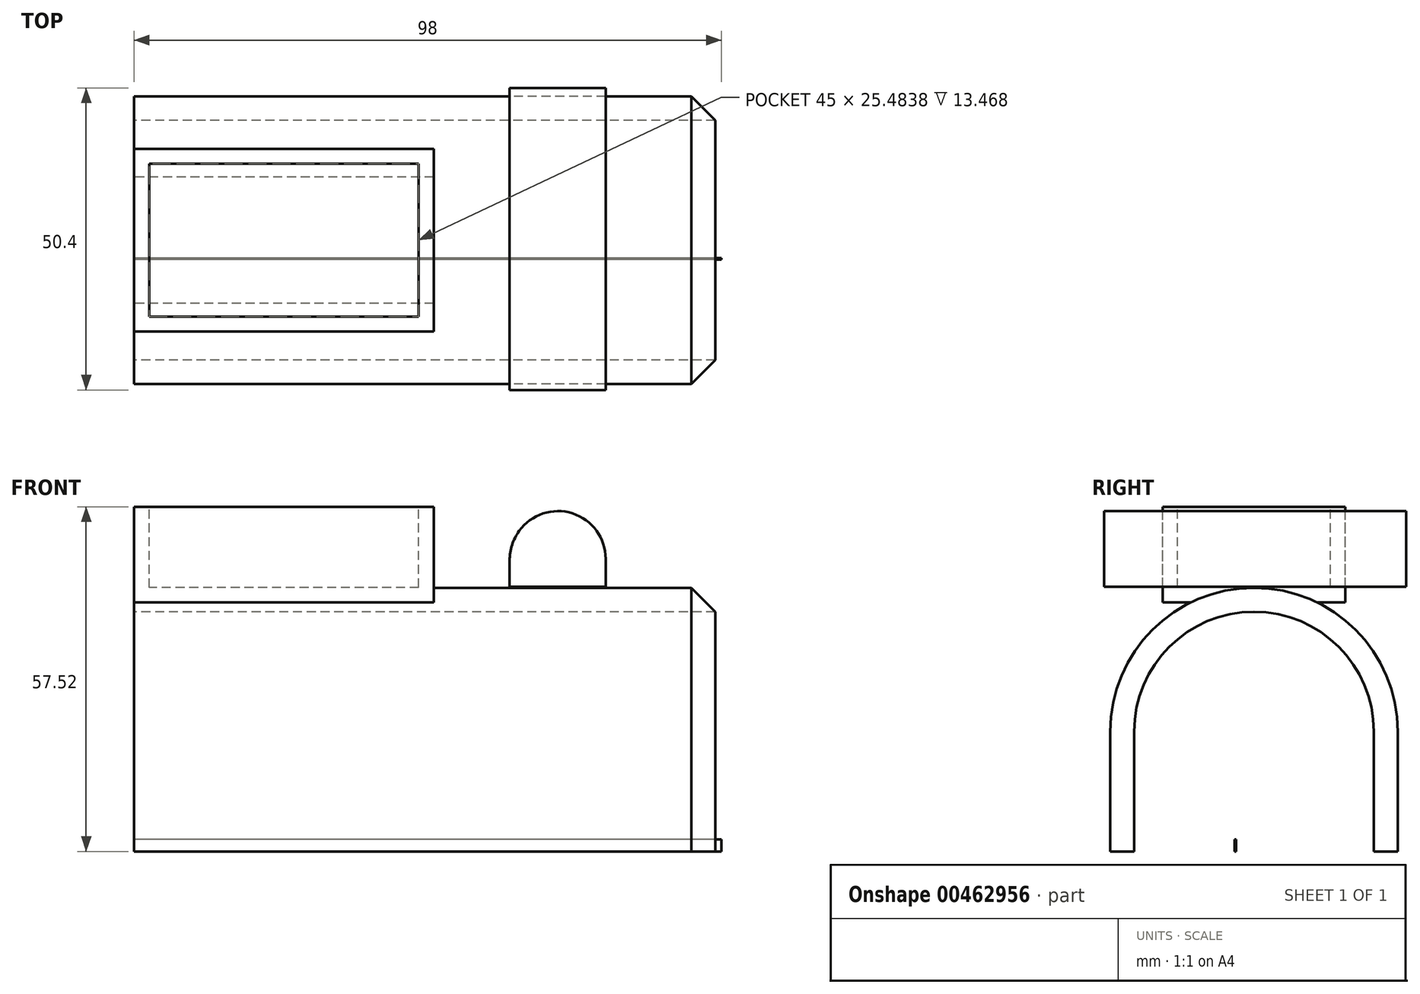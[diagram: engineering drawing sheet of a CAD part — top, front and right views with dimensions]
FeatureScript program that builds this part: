
annotation { "Feature Type Name" : "Feature", "Feature Type Description" : "" }
export const myFeature = defineFeature(function(context is Context, id is Id, definition is map)
    precondition{}
    {
        {
            var Q0;
            Q0=qCreatedBy(makeId("Right.planeOp"),FACE);
            var sketch = newSketch(context, id + "F0", { "sketchPlane" : qUnion([Q0])});
            skLineSegment(sketch, "E0.bottom", {"start": v(-3.25, 0) * mm, "end": v(-3, 0) * mm});
            skLineSegment(sketch, "E0.top", {"start": v(-3.25, 2) * mm, "end": v(-3, 2) * mm});
            skLineSegment(sketch, "E0.left", {"start": v(-3.25, 0) * mm, "end": v(-3.25, 2) * mm});
            skLineSegment(sketch, "E0.right", {"start": v(-3, 0) * mm, "end": v(-3, 2) * mm});
            skSolve(sketch);
        }
        {
            var Q0;
            Q0=qCreatedBy(makeId("Right.planeOp"),FACE);
            var sketch = newSketch(context, id + "F1", { "sketchPlane" : qUnion([Q0])});
            skLineSegment(sketch, "E1.bottom", {"start": v(-20, 0) * mm, "end": v(-24, 0) * mm});
            skLineSegment(sketch, "E1.top", {"start": v(-20, 20) * mm, "end": v(-24, 20) * mm});
            skLineSegment(sketch, "E1.left", {"start": v(-20, 0) * mm, "end": v(-20, 20) * mm});
            skLineSegment(sketch, "E1.right", {"start": v(-24, 0) * mm, "end": v(-24, 20) * mm});
            skLineSegment(sketch, "E2.MirrorCS", {"start": v(20, 0) * mm, "end": v(24, 0) * mm});
            skLineSegment(sketch, "E3.MirrorCS", {"start": v(20, 20) * mm, "end": v(24, 20) * mm});
            skLineSegment(sketch, "E4.MirrorCS", {"start": v(24, 0) * mm, "end": v(24, 20) * mm});
            skLineSegment(sketch, "E5.MirrorCS", {"start": v(20, 0) * mm, "end": v(20, 20) * mm});
            skArc(sketch, "E6", {"start": v(20, 20) * mm, "mid": v(0, 40) * mm, "end": v(-20, 20) * mm});
            skArc(sketch, "E7", {"start": v(24, 20) * mm, "mid": v(0, 44) * mm, "end": v(-24, 20) * mm});
            skSolve(sketch);
        }
        {
            var Q0;
            Q0=makeQuery(id+"F1.imprint","IMPRINT",FACE,{"disambiguationData":[TD([[makeQuery(id+"F1.imprint","IMPRINT",EDGE,{"derivedFrom":sQuery(id+"F1.wireOp",EDGE,"E1.bottom")}),-1.0]])]});
            var Q1;
            Q1=makeQuery(id+"F1.imprint","IMPRINT",FACE,{"disambiguationData":[TD([[makeQuery(id+"F1.imprint","IMPRINT",EDGE,{"derivedFrom":sQuery(id+"F1.wireOp",EDGE,"E2.MirrorCS")}),1.0]])]});
            var Q2;
            Q2=makeQuery(id+"F1.imprint","IMPRINT",FACE,{"disambiguationData":[TD([[makeQuery(id+"F1.imprint","IMPRINT",EDGE,{"derivedFrom":sQuery(id+"F1.wireOp",EDGE,"E1.top")}),-1.0]])]});
            var Q3;
            Q3=makeQuery(id+"F0.imprint","IMPRINT",FACE,{"disambiguationData":[TD([[makeQuery(id+"F0.imprint","IMPRINT",EDGE,{"derivedFrom":sQuery(id+"F0.wireOp",EDGE,"E0.bottom")}),1.0]])]});
            extrude(context, id + "F2", {"entities" : qUnion([Q0, Q1, Q2, Q3]), "depth" : 98 * mm});
        }
        {
            var Q0;
            Q0=qCreatedBy(makeId("Right.planeOp"),FACE);
            var sketch = newSketch(context, id + "F3", { "sketchPlane" : qUnion([Q0])});
            skLineSegment(sketch, "E8.bottom", {"start": v(15.24, 41.55) * mm, "end": v(-15.24, 41.55) * mm});
            skLineSegment(sketch, "E8.top", {"start": v(15.24, 57.52) * mm, "end": v(-15.24, 57.52) * mm});
            skLineSegment(sketch, "E8.left", {"start": v(15.24, 41.55) * mm, "end": v(15.24, 57.52) * mm});
            skLineSegment(sketch, "E8.right", {"start": v(-15.24, 41.55) * mm, "end": v(-15.24, 57.52) * mm});
            skPoint(sketch, "E8.middle", {"position": v(0, 49.54) * mm});
            skSolve(sketch);
        }
        {
            var Q0;
            Q0=makeQuery(id+"F2.opExtrude","CAP_EDGE",EDGE,{"disambiguationData":[OSD([sQuery(id+"F1.wireOp",EDGE,"E7")])],"isStart":false});
            chamfer(context, id + "F4", {"entities" : qUnion([Q0]), "width" : 5 * mm, "tangentPropagation" : true});
        }
        {
            var Q0;
            Q0=makeQuery(id+"F3.imprint","IMPRINT",FACE,{"disambiguationData":[TD([[makeQuery(id+"F3.imprint","IMPRINT",EDGE,{"derivedFrom":sQuery(id+"F3.wireOp",EDGE,"E8.bottom")}),-1.0]])]});
            extrude(context, id + "F5", {"entities" : qUnion([Q0]), "operationType" : NewBodyOperationType.ADD, "depth" : 25 * mm});
        }
        {
            var Q0;
            Q0=makeQuery(id+"F5.opExtrude","CAP_FACE",FACE,{"disambiguationData":[OSD([sQuery(id+"F3.wireOp",EDGE,"E8.bottom"),sQuery(id+"F3.wireOp",EDGE,"E8.top"),sQuery(id+"F3.wireOp",EDGE,"E8.left"),sQuery(id+"F3.wireOp",EDGE,"E8.right")])],"isStart":false});
            extrude(context, id + "F6", {"entities" : qUnion([Q0]), "operationType" : NewBodyOperationType.ADD, "depth" : 25 * mm});
        }
        {
            var Q0;
            {var subQ0=sQuery(id+"F3.wireOp",EDGE,"E8.top");Q0=makeQuery(id+"F6.boolean.opBoolean","MERGE",FACE,{"derivedFrom":[makeQuery(id+"F5.opExtrude","SWEPT_FACE",FACE,{"disambiguationData":[OSD([subQ0])]}),makeQuery(id+"F6.opExtrude","SWEPT_FACE",FACE,{"disambiguationData":[OSD([subQ0])]})]});}
            shell(context, id + "F7", {"entities" : qUnion([Q0]), "thickness" : 2.5 * mm});
        }
        {
            var Q0;
            Q0=qCreatedBy(makeId("Front.planeOp"),FACE);
            cPlane(context, id + "F8", {"entities" : qUnion([Q0]), "cplaneType" : CPlaneType.OFFSET, "offset" : 25 * mm, "width" : 150 * mm, "height" : 150 * mm});
        }
        {
            var Q0;
            Q0=qCreatedBy(id+"F8.planeOp",FACE);
            var sketch = newSketch(context, id + "F9", { "sketchPlane" : qUnion([Q0])});
            skLineSegment(sketch, "E9.bottom", {"start": v(62.66, 57) * mm, "end": v(78.69, 57) * mm});
            skLineSegment(sketch, "E9.top", {"start": v(62.66, 44.18) * mm, "end": v(78.69, 44.18) * mm});
            skLineSegment(sketch, "E9.left", {"start": v(62.66, 57) * mm, "end": v(62.66, 44.18) * mm});
            skLineSegment(sketch, "E9.right", {"start": v(78.69, 57) * mm, "end": v(78.69, 44.18) * mm});
            skPoint(sketch, "E9.middle", {"position": v(70.68, 50.6) * mm});
            skSolve(sketch);
        }
        {
            var Q0;
            Q0=makeQuery(id+"F9.imprint","IMPRINT",FACE,{"disambiguationData":[TD([[makeQuery(id+"F9.imprint","IMPRINT",EDGE,{"derivedFrom":sQuery(id+"F9.wireOp",EDGE,"E9.bottom")}),-1.0]])]});
            extrude(context, id + "F10", {"entities" : qUnion([Q0]), "oppositeDirection" : true, "depth" : 50.4 * mm});
        }
        {
            var Q0;
            Q0=makeQuery(id+"F10.opExtrude","SWEPT_EDGE",EDGE,{"disambiguationData":[OSD([sQuery(id+"F9.wireOp",EDGE,"E9.bottom"),sQuery(id+"F9.wireOp",EDGE,"E9.left")])]});
            fillet(context, id + "F11", {"entities" : qUnion([Q0]), "radius" : 8.45 * mm, "tangentPropagation" : true, "allowEdgeOverflow" : false});
        }
        {
            var Q0;
            Q0=makeQuery(id+"F10.opExtrude","SWEPT_EDGE",EDGE,{"disambiguationData":[OSD([sQuery(id+"F9.wireOp",EDGE,"E9.bottom"),sQuery(id+"F9.wireOp",EDGE,"E9.right")])]});
            fillet(context, id + "F12", {"entities" : qUnion([Q0]), "radius" : 7.97 * mm, "tangentPropagation" : true, "allowEdgeOverflow" : false});
        }
    });
